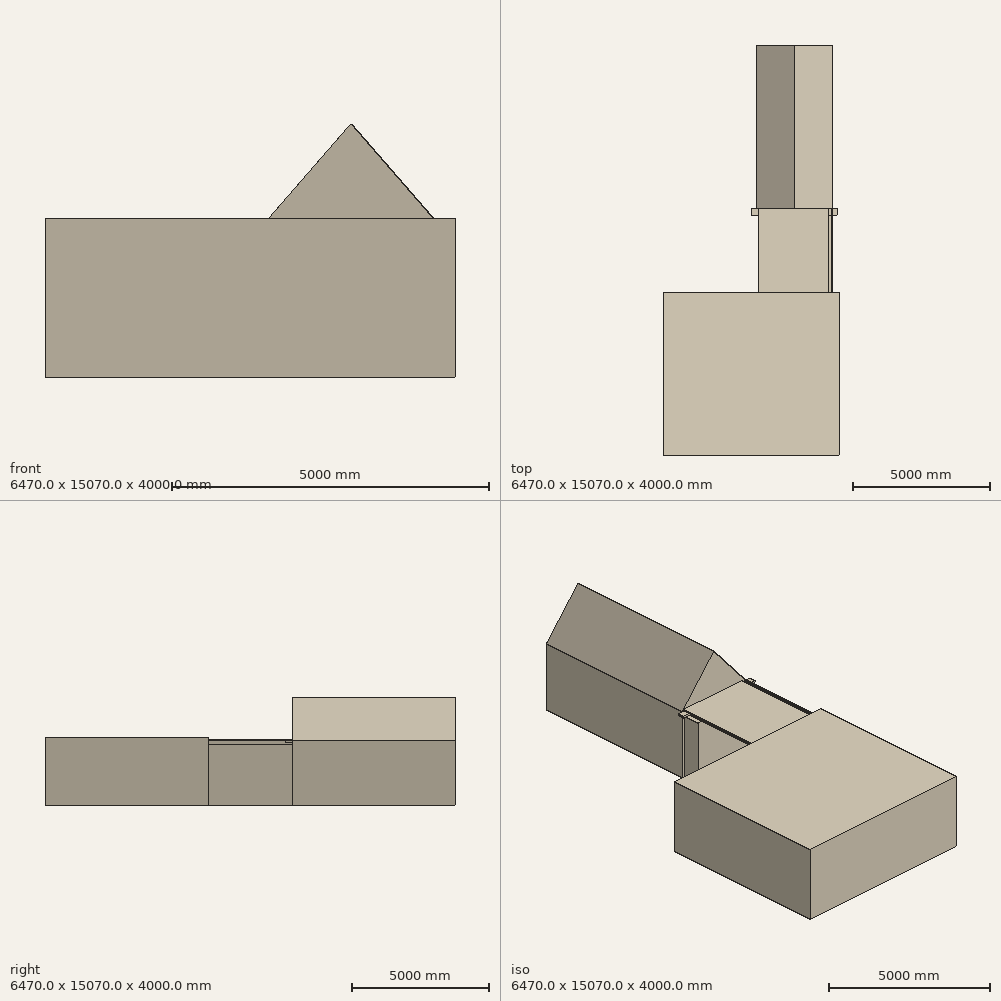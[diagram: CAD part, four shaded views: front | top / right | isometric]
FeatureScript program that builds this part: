
annotation { "Feature Type Name" : "Feature", "Feature Type Description" : "" }
export const myFeature = defineFeature(function(context is Context, id is Id, definition is map)
    precondition{}
    {
        {
            var Q0;
            Q0=qCreatedBy(makeId("Front.planeOp"),FACE);
            var sketch = newSketch(context, id + "F0", { "sketchPlane" : qUnion([Q0])});
            skLineSegment(sketch, "E0.bottom", {"start": v(-2655, 0) * mm, "end": v(0, 0) * mm});
            skLineSegment(sketch, "E0.left", {"start": v(0, 0) * mm, "end": v(0, 2330) * mm, "construction": true});
            skLineSegment(sketch, "E0.right", {"start": v(-2655, 0) * mm, "end": v(-2655, 2330) * mm});
            skLineSegment(sketch, "E1.top", {"start": v(0, 0) * mm, "end": v(145, 0) * mm});
            skLineSegment(sketch, "E1.right", {"start": v(145, 2330) * mm, "end": v(145, 0) * mm});
            skLineSegment(sketch, "E2", {"start": v(-2655, 2330) * mm, "end": v(145, 2330) * mm, "construction": true});
            skLineSegment(sketch, "E3", {"start": v(-1255, 4000) * mm, "end": v(-1255, 0) * mm, "construction": true});
            skPoint(sketch, "E4", {"position": v(-1255, 2330) * mm});
            skLineSegment(sketch, "E5.top", {"start": v(-2655, 2390) * mm, "end": v(-2490, 2390) * mm, "construction": true});
            skLineSegment(sketch, "E5.left", {"start": v(-2655, 2330) * mm, "end": v(-2655, 2390) * mm});
            skLineSegment(sketch, "E5.right", {"start": v(-2490, 2330) * mm, "end": v(-2490, 2390) * mm, "construction": true});
            skLineSegment(sketch, "E6.MirrorCS", {"start": v(145, 2390) * mm, "end": v(-20, 2390) * mm, "construction": true});
            skLineSegment(sketch, "E7.MirrorCS", {"start": v(-20, 2330) * mm, "end": v(-20, 2390) * mm, "construction": true});
            skLineSegment(sketch, "E8.MirrorCS", {"start": v(145, 2330) * mm, "end": v(145, 2390) * mm});
            skLineSegment(sketch, "E9", {"start": v(-2655, 2390) * mm, "end": v(-1255, 4000) * mm});
            skLineSegment(sketch, "E10.MirrorCS", {"start": v(145, 2390) * mm, "end": v(-1255, 4000) * mm});
            skSolve(sketch);
        }
        {
            var Q0;
            Q0 = qSketchRegion(id + "F0", true);
            extrude(context, id + "F1", {"entities" : qUnion([Q0]), "oppositeDirection" : true, "depth" : 6000 * mm, "offsetDistance" : 25 * mm});
        }
        {
            var Q0;
            Q0=makeQuery(id+"F0.imprint","IMPRINT",FACE,{"disambiguationData":[TD([[makeQuery(id+"F0.imprint","IMPRINT",EDGE,{"derivedFrom":sQuery(id+"F0.wireOp",EDGE,"E0.bottom")}),1.0]])]});
            var sketch = newSketch(context, id + "F2", { "sketchPlane" : qUnion([Q0])});
            skLineSegment(sketch, "E11.bottom", {"start": v(-2655, 2390) * mm, "end": v(-2490, 2390) * mm});
            skLineSegment(sketch, "E11.top", {"start": v(-2655, 2330) * mm, "end": v(-2490, 2330) * mm});
            skLineSegment(sketch, "E11.left", {"start": v(-2655, 2390) * mm, "end": v(-2655, 2330) * mm, "construction": true});
            skLineSegment(sketch, "E11.right", {"start": v(-2490, 2390) * mm, "end": v(-2490, 2330) * mm});
            skLineSegment(sketch, "E12", {"start": v(-2655, 2390) * mm, "end": v(-2830, 2390) * mm});
            skLineSegment(sketch, "E13", {"start": v(-2830, 2390) * mm, "end": v(-2830, 2330) * mm});
            skLineSegment(sketch, "E14", {"start": v(-2830, 2330) * mm, "end": v(-2655, 2330) * mm});
            skLineSegment(sketch, "E15", {"start": v(-1255, 4000) * mm, "end": v(-1255, 0) * mm, "construction": true});
            skLineSegment(sketch, "E16.MirrorCS", {"start": v(145, 2390) * mm, "end": v(145, 2330) * mm, "construction": true});
            skLineSegment(sketch, "E17.MirrorCS", {"start": v(320, 2390) * mm, "end": v(320, 2330) * mm});
            skLineSegment(sketch, "E18.MirrorCS", {"start": v(-20, 2390) * mm, "end": v(-20, 2330) * mm});
            skLineSegment(sketch, "E19.MirrorCS", {"start": v(320, 2330) * mm, "end": v(145, 2330) * mm});
            skLineSegment(sketch, "E20.MirrorCS", {"start": v(145, 2330) * mm, "end": v(-20, 2330) * mm});
            skLineSegment(sketch, "E21.MirrorCS", {"start": v(145, 2390) * mm, "end": v(320, 2390) * mm});
            skLineSegment(sketch, "E22.MirrorCS", {"start": v(145, 2390) * mm, "end": v(-20, 2390) * mm});
            skSolve(sketch);
        }
        {
            var Q0;
            Q0 = qSketchRegion(id + "F2", true);
            extrude(context, id + "F3", {"entities" : qUnion([Q0]), "operationType" : NewBodyOperationType.ADD, "depth" : 240 * mm, "offsetDistance" : 25 * mm});
        }
        {
            var Q0;
            Q0=makeQuery(id+"F1.opExtrude","CAP_FACE",FACE,{"disambiguationData":[OSD([sQuery(id+"F0.wireOp",EDGE,"E0.bottom"),sQuery(id+"F0.wireOp",EDGE,"E0.right"),sQuery(id+"F0.wireOp",EDGE,"E1.top"),sQuery(id+"F0.wireOp",EDGE,"E1.right"),sQuery(id+"F0.wireOp",EDGE,"1YgyDX2S-HBrp-eld6-nWvb-rL9RVo18pb6X"),sQuery(id+"F0.wireOp",EDGE,"aHWsKlSm-hkMd-Fo63-juqk-muZd2j0DPrLM")])],"isStart":true});
            var sketch = newSketch(context, id + "F4", { "sketchPlane" : qUnion([Q0])});
            skLineSegment(sketch, "E23.bottom", {"start": v(0, 0) * mm, "end": v(80, 0) * mm});
            skLineSegment(sketch, "E23.left", {"start": v(0, 0) * mm, "end": v(0, 1800) * mm});
            skLineSegment(sketch, "E23.right", {"start": v(80, 0) * mm, "end": v(80, 1800) * mm});
            skLineSegment(sketch, "E24.bottom", {"start": v(80, 1800) * mm, "end": v(0, 1800) * mm, "construction": true});
            skLineSegment(sketch, "E24.top", {"start": v(80, 2330) * mm, "end": v(0, 2330) * mm});
            skLineSegment(sketch, "E24.left", {"start": v(80, 1800) * mm, "end": v(80, 2330) * mm});
            skLineSegment(sketch, "E24.right", {"start": v(0, 1800) * mm, "end": v(0, 2330) * mm});
            skSolve(sketch);
        }
        {
            var Q0;
            Q0 = qSketchRegion(id + "F4", true);
            extrude(context, id + "F5", {"entities" : qUnion([Q0]), "depth" : 3070 * mm, "offsetDistance" : 25 * mm});
        }
        {
            var Q0;
            Q0=makeQuery(id+"F5.opExtrude","CAP_FACE",FACE,{"disambiguationData":[OSD([sQuery(id+"F4.wireOp",EDGE,"E23.bottom"),sQuery(id+"F4.wireOp",EDGE,"E23.top"),sQuery(id+"F4.wireOp",EDGE,"E23.left"),sQuery(id+"F4.wireOp",EDGE,"E23.right")])],"isStart":false});
            var sketch = newSketch(context, id + "F6", { "sketchPlane" : qUnion([Q0])});
            skLineSegment(sketch, "E25.bottom", {"start": v(390, 0) * mm, "end": v(-3080, 0) * mm});
            skLineSegment(sketch, "E25.top", {"start": v(390, 2510) * mm, "end": v(-3080, 2510) * mm});
            skLineSegment(sketch, "E25.left", {"start": v(390, 0) * mm, "end": v(390, 2510) * mm});
            skLineSegment(sketch, "E26.bottom", {"start": v(-3080, 2510) * mm, "end": v(-6080, 2510) * mm});
            skLineSegment(sketch, "E26.top", {"start": v(-3080, 0) * mm, "end": v(-6080, 0) * mm});
            skLineSegment(sketch, "E26.left", {"start": v(-3080, 2510) * mm, "end": v(-3080, 0) * mm, "construction": true});
            skLineSegment(sketch, "E26.right", {"start": v(-6080, 2510) * mm, "end": v(-6080, 0) * mm});
            skSolve(sketch);
        }
        {
            var Q0;
            Q0 = qSketchRegion(id + "F6", true);
            extrude(context, id + "F7", {"entities" : qUnion([Q0]), "depth" : 6000 * mm, "offsetDistance" : 25 * mm});
        }
        {
            var Q0;
            Q0=makeQuery(id+"F1.opExtrude","CAP_FACE",FACE,{"disambiguationData":[OSD([sQuery(id+"F0.wireOp",EDGE,"E0.bottom"),sQuery(id+"F0.wireOp",EDGE,"E0.right"),sQuery(id+"F0.wireOp",EDGE,"E1.top"),sQuery(id+"F0.wireOp",EDGE,"E1.right"),sQuery(id+"F0.wireOp",EDGE,"1YgyDX2S-HBrp-eld6-nWvb-rL9RVo18pb6X"),sQuery(id+"F0.wireOp",EDGE,"aHWsKlSm-hkMd-Fo63-juqk-muZd2j0DPrLM")])],"isStart":true});
            var sketch = newSketch(context, id + "F8", { "sketchPlane" : qUnion([Q0])});
            skLineSegment(sketch, "E27", {"start": v(-2602.83, 2450) * mm, "end": v(0, 2430) * mm});
            skLineSegment(sketch, "E28", {"start": v(0, 2430) * mm, "end": v(-0.18, 2406) * mm});
            skLineSegment(sketch, "E29", {"start": v(-0.18, 2406) * mm, "end": v(-2603.01, 2426) * mm});
            skLineSegment(sketch, "E30", {"start": v(-2602.83, 2450) * mm, "end": v(-2603.01, 2426) * mm});
            skSolve(sketch);
        }
        {
            var Q0;
            Q0 = qSketchRegion(id + "F8", true);
            var Q1;
            Q1=makeQuery(id+"F7.opExtrude","SWEPT_BODY",BODY,{"disambiguationData":[OSD([sQuery(id+"F6.wireOp",EDGE,"E25.bottom"),sQuery(id+"F6.wireOp",EDGE,"E25.top"),sQuery(id+"F6.wireOp",EDGE,"E25.left"),sQuery(id+"F6.wireOp",EDGE,"E25.right")])]});
            extrude(context, id + "F9", {"entities" : qUnion([Q0]), "endBound" : BoundingType.UP_TO_BODY, "depth" : 25 * mm, "endBoundEntityBody" : qUnion([Q1]), "offsetDistance" : 25 * mm});
        }
        {
            var Q0;
            Q0=makeQuery(id+"F1.opExtrude","CAP_FACE",FACE,{"disambiguationData":[OSD([sQuery(id+"F0.wireOp",EDGE,"E0.bottom"),sQuery(id+"F0.wireOp",EDGE,"E0.right"),sQuery(id+"F0.wireOp",EDGE,"E1.top"),sQuery(id+"F0.wireOp",EDGE,"E1.right"),sQuery(id+"F0.wireOp",EDGE,"1YgyDX2S-HBrp-eld6-nWvb-rL9RVo18pb6X"),sQuery(id+"F0.wireOp",EDGE,"aHWsKlSm-hkMd-Fo63-juqk-muZd2j0DPrLM")])],"isStart":true});
            var sketch = newSketch(context, id + "F10", { "sketchPlane" : qUnion([Q0])});
            skLineSegment(sketch, "E31.bottom", {"start": v(-2435, 2424.7) * mm, "end": v(-2490, 2424.7) * mm});
            skLineSegment(sketch, "E31.top", {"start": v(-2435, 2269.7) * mm, "end": v(-2490, 2269.7) * mm});
            skLineSegment(sketch, "E31.left", {"start": v(-2435, 2424.7) * mm, "end": v(-2435, 2269.7) * mm});
            skLineSegment(sketch, "E31.right", {"start": v(-2490, 2424.7) * mm, "end": v(-2490, 2269.7) * mm});
            skLineSegment(sketch, "E32.bottom", {"start": v(-1835, 2420.1) * mm, "end": v(-1890, 2420.1) * mm});
            skLineSegment(sketch, "E32.top", {"start": v(-1835, 2265.1) * mm, "end": v(-1890, 2265.1) * mm});
            skLineSegment(sketch, "E32.left", {"start": v(-1835, 2420.1) * mm, "end": v(-1835, 2265.1) * mm});
            skLineSegment(sketch, "E32.right", {"start": v(-1890, 2420.1) * mm, "end": v(-1890, 2265.1) * mm});
            skLineSegment(sketch, "E33.bottom", {"start": v(-35, 2406.27) * mm, "end": v(-90, 2406.27) * mm});
            skLineSegment(sketch, "E33.top", {"start": v(-35, 2251.27) * mm, "end": v(-90, 2251.27) * mm});
            skLineSegment(sketch, "E33.left", {"start": v(-35, 2406.27) * mm, "end": v(-35, 2251.27) * mm});
            skLineSegment(sketch, "E33.right", {"start": v(-90, 2406.27) * mm, "end": v(-90, 2251.27) * mm});
            skLineSegment(sketch, "E34.bottom", {"start": v(-635, 2410.88) * mm, "end": v(-690, 2410.88) * mm});
            skLineSegment(sketch, "E34.top", {"start": v(-635, 2255.88) * mm, "end": v(-690, 2255.88) * mm});
            skLineSegment(sketch, "E34.left", {"start": v(-635, 2410.88) * mm, "end": v(-635, 2255.88) * mm});
            skLineSegment(sketch, "E34.right", {"start": v(-690, 2410.88) * mm, "end": v(-690, 2255.88) * mm});
            skLineSegment(sketch, "E35.bottom", {"start": v(-1235, 2415.49) * mm, "end": v(-1290, 2415.49) * mm});
            skLineSegment(sketch, "E35.top", {"start": v(-1235, 2260.49) * mm, "end": v(-1290, 2260.49) * mm});
            skLineSegment(sketch, "E35.left", {"start": v(-1235, 2415.49) * mm, "end": v(-1235, 2260.49) * mm});
            skLineSegment(sketch, "E35.right", {"start": v(-1290, 2415.49) * mm, "end": v(-1290, 2260.49) * mm});
            skLineSegment(sketch, "E36.bottom", {"start": v(145, 2404.89) * mm, "end": v(90, 2404.89) * mm});
            skLineSegment(sketch, "E36.top", {"start": v(145, 2249.89) * mm, "end": v(90, 2249.89) * mm});
            skLineSegment(sketch, "E36.left", {"start": v(145, 2404.89) * mm, "end": v(145, 2249.89) * mm});
            skLineSegment(sketch, "E36.right", {"start": v(90, 2404.89) * mm, "end": v(90, 2249.89) * mm});
            skSolve(sketch);
        }
        {
            var Q0;
            Q0 = qSketchRegion(id + "F10", true);
            var Q1;
            Q1=makeQuery(id+"F7.opExtrude","SWEPT_BODY",BODY,{"disambiguationData":[OSD([sQuery(id+"F6.wireOp",EDGE,"E25.bottom"),sQuery(id+"F6.wireOp",EDGE,"E25.top"),sQuery(id+"F6.wireOp",EDGE,"E25.left"),sQuery(id+"F6.wireOp",EDGE,"E25.right")])]});
            extrude(context, id + "F11", {"entities" : qUnion([Q0]), "endBound" : BoundingType.UP_TO_BODY, "depth" : 25 * mm, "endBoundEntityBody" : qUnion([Q1]), "offsetDistance" : 25 * mm});
        }
        {
            var Q0;
            Q0=makeQuery(id+"F1.opExtrude","CAP_FACE",FACE,{"disambiguationData":[OSD([sQuery(id+"F0.wireOp",EDGE,"E0.bottom"),sQuery(id+"F0.wireOp",EDGE,"E0.right"),sQuery(id+"F0.wireOp",EDGE,"E1.top"),sQuery(id+"F0.wireOp",EDGE,"E1.right"),sQuery(id+"F0.wireOp",EDGE,"E5.left"),sQuery(id+"F0.wireOp",EDGE,"E9"),sQuery(id+"F0.wireOp",EDGE,"E8.MirrorCS"),sQuery(id+"F0.wireOp",EDGE,"E10.MirrorCS")])],"isStart":true});
            var sketch = newSketch(context, id + "F12", { "sketchPlane" : qUnion([Q0])});
            skLineSegment(sketch, "E37.bottom", {"start": v(-2544, 0) * mm, "end": v(0, 0) * mm});
            skLineSegment(sketch, "E37.top", {"start": v(-2544, 2180) * mm, "end": v(0, 2180) * mm});
            skLineSegment(sketch, "E37.left", {"start": v(-2544, 0) * mm, "end": v(-2544, 2180) * mm});
            skLineSegment(sketch, "E37.right", {"start": v(0, 0) * mm, "end": v(0, 2180) * mm});
            skSolve(sketch);
        }
        {
            var Q0;
            Q0 = qSketchRegion(id + "F12", true);
            extrude(context, id + "F13", {"entities" : qUnion([Q0]), "depth" : 600 * mm, "offsetDistance" : 25 * mm});
        }
    });
